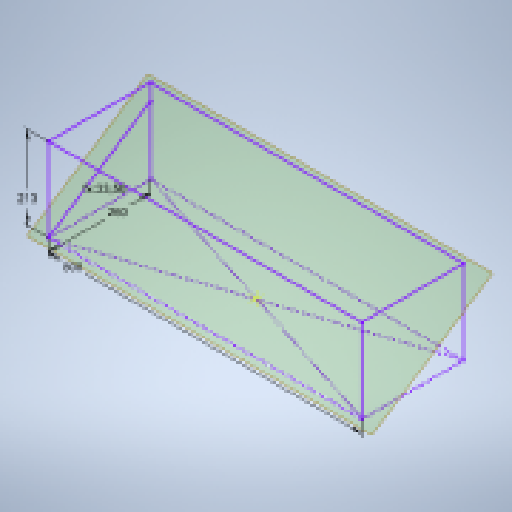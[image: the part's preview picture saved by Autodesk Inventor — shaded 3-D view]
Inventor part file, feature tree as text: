
AUTODESK INVENTOR PART (.ipt)
format: ipt  version: 2025 (Build 290162010, 162A)  size: 137,728 bytes
history: native  units: in
note: dims shown in document units (in); Inventor stores cm internally (conversion verified against a paired STEP export)
features: other x4, sketch x2, plane x2
ambient origin geometry x8: Origin, YZ Plane, XZ Plane, XY Plane, X Axis, Y Axis, Z Axis, Center Point
feature tree (8):
  sketch  "Sketch3"  dims[d4=10.2362in d5=31.4961in d11=8.3858in d12=0.2302in d13=90.0deg]
  sketch  "3D Sketch3"
  plane  "Work Plane3"
  plane  "Work Plane2"
  other  "<userpath>\Documents\Inventor\NDM-VOS_powder_hopper\ASY_Ступень.iam"
  other  "ASY_Ступень.iam"
  other  "Frame 1730738645257:1"
  other  "ISO 4019 - 40x20x2 - 142,05:1"
